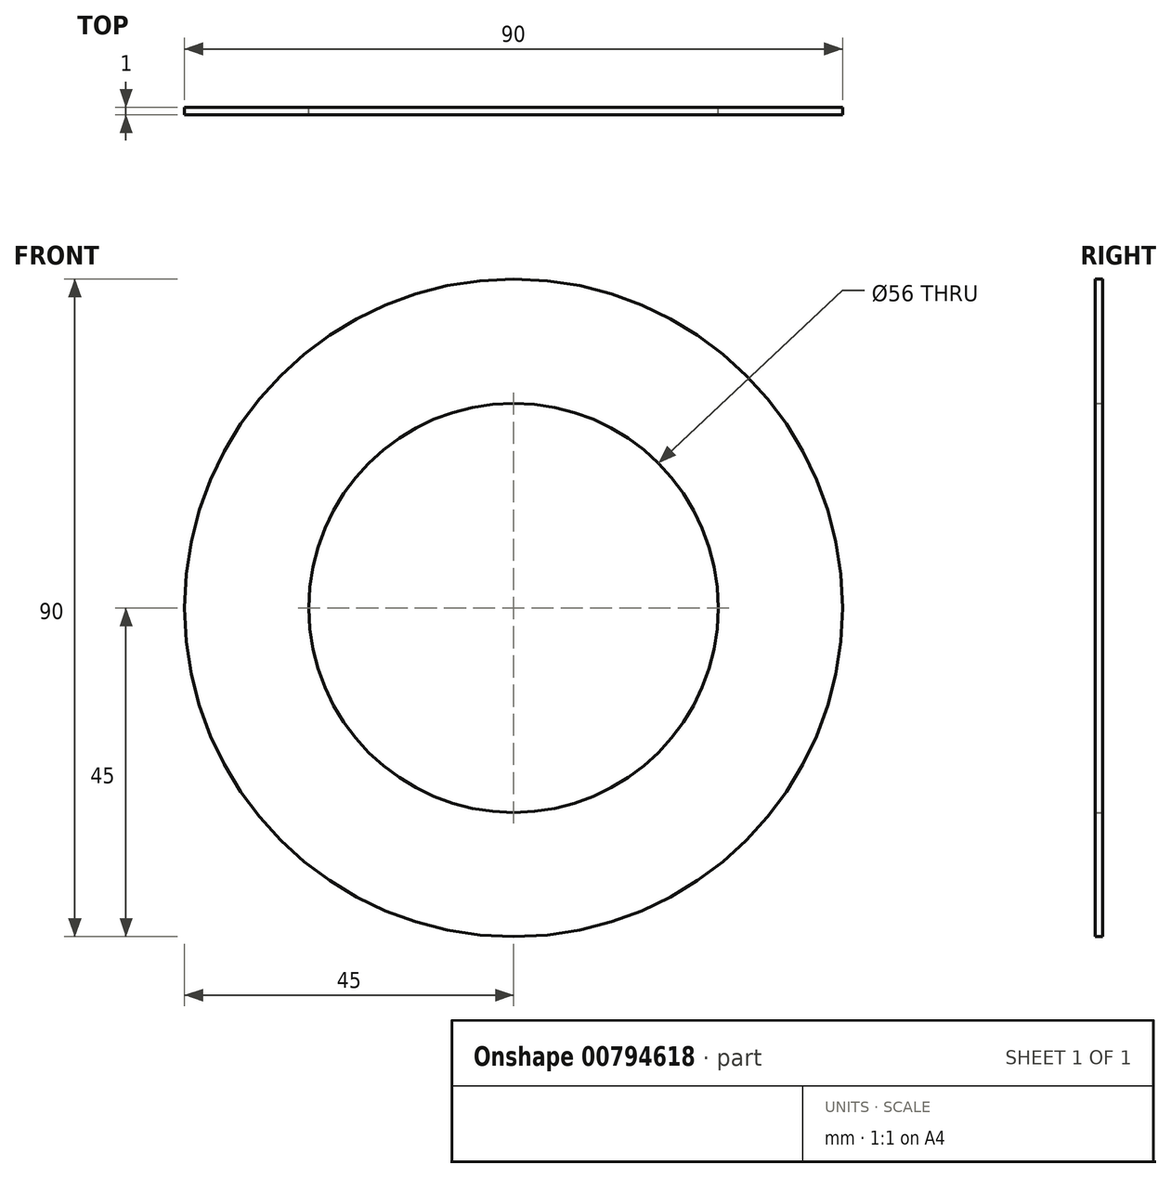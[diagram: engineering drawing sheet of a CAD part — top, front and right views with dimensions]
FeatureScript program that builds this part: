
annotation { "Feature Type Name" : "Feature", "Feature Type Description" : "" }
export const myFeature = defineFeature(function(context is Context, id is Id, definition is map)
    precondition{}
    {
        {
            var Q0;
            Q0=qCreatedBy(makeId("Front.planeOp"),FACE);
            var sketch = newSketch(context, id + "F0", { "sketchPlane" : qUnion([Q0])});
            skCircle(sketch, "E0", {"center": v(0, 0) * mm, "radius": 28 * mm});
            skCircle(sketch, "E1", {"center": v(0, 0) * mm, "radius": 45 * mm});
            skSolve(sketch);
        }
        {
            var Q0;
            Q0 = qSketchRegion(id + "F0", true);
            extrude(context, id + "F1", {"entities" : qUnion([Q0]), "depth" : 1 * mm, "offsetDistance" : 25 * mm});
        }
    });
